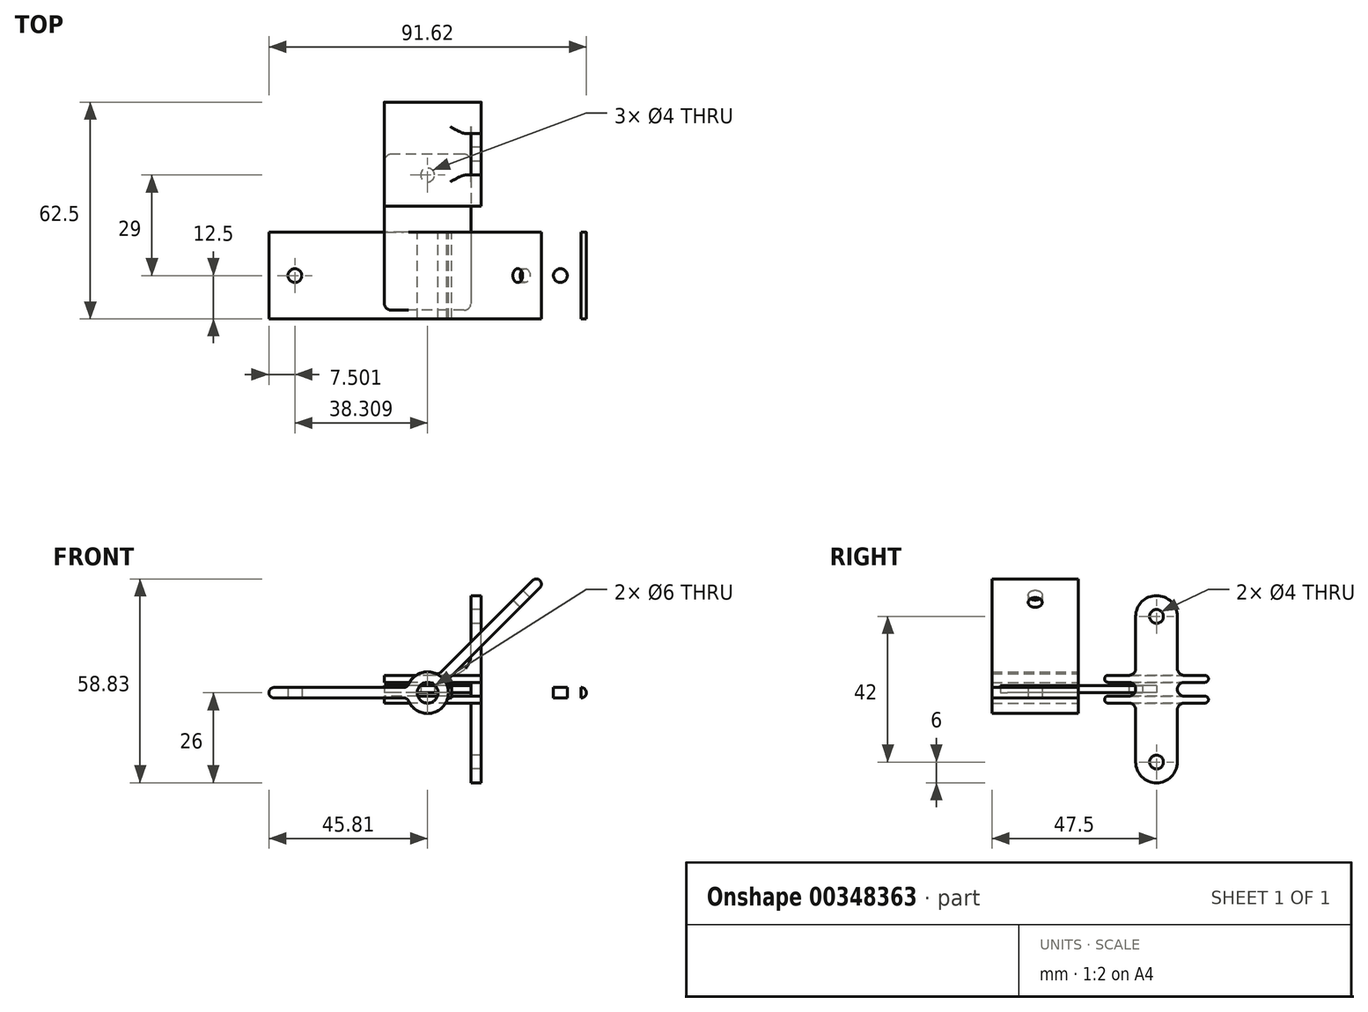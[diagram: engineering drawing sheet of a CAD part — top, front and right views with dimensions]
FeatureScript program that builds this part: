
annotation { "Feature Type Name" : "Feature", "Feature Type Description" : "" }
export const myFeature = defineFeature(function(context is Context, id is Id, definition is map)
    precondition{}
    {
        {
            var Q0;
            Q0=qCreatedBy(makeId("Front.planeOp"),FACE);
            var sketch = newSketch(context, id + "F0", { "sketchPlane" : qUnion([Q0])});
            skCircle(sketch, "E0", {"center": v(0, 0) * mm, "radius": 3 * mm});
            skCircle(sketch, "E1", {"center": v(0, 0) * mm, "radius": 6 * mm});
            skLineSegment(sketch, "E2", {"start": v(-5.8, 1.5) * mm, "end": v(-45.8, 1.5) * mm});
            skLineSegment(sketch, "E3", {"start": v(-45.8, 1.5) * mm, "end": v(-45.8, -1.5) * mm});
            skLineSegment(sketch, "E4", {"start": v(-45.8, -1.5) * mm, "end": v(-5.8, -1.5) * mm});
            skLineSegment(sketch, "E5.MirrorCS", {"start": v(45.8, -1.5) * mm, "end": v(5.8, -1.5) * mm});
            skLineSegment(sketch, "E6.MirrorCS", {"start": v(45.8, 1.5) * mm, "end": v(45.8, -1.5) * mm});
            skLineSegment(sketch, "E7.MirrorCS", {"start": v(5.8, 1.5) * mm, "end": v(45.8, 1.5) * mm});
            skSolve(sketch);
        }
        {
            var Q0;
            {var subQ0=sQuery(id+"F0.wireOp",EDGE,"E2");Q0=makeQuery(id+"F0.imprint","IMPRINT",FACE,{"disambiguationData":[TD([[makeQuery(id+"F0.imprint","IMPRINT",EDGE,{"derivedFrom":subQ0}),1.0]])]});}
            var Q1;
            Q1=makeQuery(id+"F0.imprint","IMPRINT",FACE,{"disambiguationData":[TD([[makeQuery(id+"F0.imprint","IMPRINT",EDGE,{"derivedFrom":sQuery(id+"F0.wireOp",EDGE,"E0")}),-1.0]])]});
            var Q2;
            {var subQ0=sQuery(id+"F0.wireOp",EDGE,"E5.MirrorCS");Q2=makeQuery(id+"F0.imprint","IMPRINT",FACE,{"disambiguationData":[TD([[makeQuery(id+"F0.imprint","IMPRINT",EDGE,{"derivedFrom":subQ0}),-1.0]])]});}
            extrude(context, id + "F1", {"entities" : qUnion([Q0, Q1, Q2]), "depth" : 25 * mm});
        }
        {
            var Q0;
            Q0=makeQuery(id+"F1.opExtrude","SWEPT_EDGE",EDGE,{"disambiguationData":[OSD([sQuery(id+"F0.wireOp",EDGE,"E2"),sQuery(id+"F0.wireOp",EDGE,"E3")])]});
            var Q1;
            Q1=makeQuery(id+"F1.opExtrude","SWEPT_EDGE",EDGE,{"disambiguationData":[OSD([sQuery(id+"F0.wireOp",EDGE,"E3"),sQuery(id+"F0.wireOp",EDGE,"E4")])]});
            var Q2;
            Q2=makeQuery(id+"F1.opExtrude","SWEPT_EDGE",EDGE,{"disambiguationData":[OSD([sQuery(id+"F0.wireOp",EDGE,"E6.MirrorCS"),sQuery(id+"F0.wireOp",EDGE,"E7.MirrorCS")])]});
            var Q3;
            Q3=makeQuery(id+"F1.opExtrude","SWEPT_EDGE",EDGE,{"disambiguationData":[OSD([sQuery(id+"F0.wireOp",EDGE,"E5.MirrorCS"),sQuery(id+"F0.wireOp",EDGE,"E6.MirrorCS")])]});
            var Q4;
            Q4=makeQuery(id+"F1.opExtrude","SWEPT_EDGE",EDGE,{"disambiguationData":[OSD([sQuery(id+"F0.wireOp",EDGE,"E1"),sQuery(id+"F0.wireOp",EDGE,"E2")])]});
            var Q5;
            Q5=makeQuery(id+"F1.opExtrude","SWEPT_EDGE",EDGE,{"disambiguationData":[OSD([sQuery(id+"F0.wireOp",EDGE,"E1"),sQuery(id+"F0.wireOp",EDGE,"E7.MirrorCS")])]});
            var Q6;
            Q6=makeQuery(id+"F1.opExtrude","SWEPT_EDGE",EDGE,{"disambiguationData":[OSD([sQuery(id+"F0.wireOp",EDGE,"E1"),sQuery(id+"F0.wireOp",EDGE,"E4")])]});
            var Q7;
            Q7=makeQuery(id+"F1.opExtrude","SWEPT_EDGE",EDGE,{"disambiguationData":[OSD([sQuery(id+"F0.wireOp",EDGE,"E1"),sQuery(id+"F0.wireOp",EDGE,"E5.MirrorCS")])]});
            fillet(context, id + "F2", {"entities" : qUnion([Q0, Q1, Q2, Q3, Q4, Q5, Q6, Q7]), "radius" : 1.5 * mm, "tangentPropagation" : true, "allowEdgeOverflow" : false});
        }
        {
            var Q0;
            Q0=qCreatedBy(makeId("Front.planeOp"),FACE);
            var sketch = newSketch(context, id + "F3", { "sketchPlane" : qUnion([Q0])});
            skCircle(sketch, "E8", {"center": v(0, 0) * mm, "radius": 3 * mm});
            skCircle(sketch, "E9", {"center": v(0, 0) * mm, "radius": 6 * mm});
            skLineSegment(sketch, "E10", {"start": v(-5.8, 1.5) * mm, "end": v(-45.8, 1.5) * mm});
            skLineSegment(sketch, "E11", {"start": v(-45.8, 1.5) * mm, "end": v(-45.8, -1.5) * mm});
            skLineSegment(sketch, "E12", {"start": v(-45.8, -1.5) * mm, "end": v(-5.8, -1.5) * mm});
            skLineSegment(sketch, "E13", {"start": v(0, 0) * mm, "end": v(32.4, 32.4) * mm, "construction": true});
            skLineSegment(sketch, "E14", {"start": v(3.05, 5.17) * mm, "end": v(31.33, 33.45) * mm});
            skLineSegment(sketch, "E15", {"start": v(31.33, 33.45) * mm, "end": v(33.45, 31.33) * mm});
            skLineSegment(sketch, "E16", {"start": v(33.45, 31.33) * mm, "end": v(5.17, 3.05) * mm});
            skSolve(sketch);
        }
        {
            var Q0;
            {var subQ0=sQuery(id+"F3.wireOp",EDGE,"E10");Q0=makeQuery(id+"F3.imprint","IMPRINT",FACE,{"disambiguationData":[TD([[makeQuery(id+"F3.imprint","IMPRINT",EDGE,{"derivedFrom":subQ0}),1.0]])]});}
            var Q1;
            Q1=makeQuery(id+"F3.imprint","IMPRINT",FACE,{"disambiguationData":[TD([[makeQuery(id+"F3.imprint","IMPRINT",EDGE,{"derivedFrom":sQuery(id+"F3.wireOp",EDGE,"E8")}),-1.0]])]});
            var Q2;
            {var subQ0=sQuery(id+"F3.wireOp",EDGE,"E14");Q2=makeQuery(id+"F3.imprint","IMPRINT",FACE,{"disambiguationData":[TD([[makeQuery(id+"F3.imprint","IMPRINT",EDGE,{"derivedFrom":subQ0}),-1.0]])]});}
            extrude(context, id + "F4", {"entities" : qUnion([Q0, Q1, Q2]), "depth" : 25 * mm});
        }
        {
            var Q0;
            Q0=makeQuery(id+"F4.opExtrude","SWEPT_EDGE",EDGE,{"disambiguationData":[OSD([sQuery(id+"F3.wireOp",EDGE,"E10"),sQuery(id+"F3.wireOp",EDGE,"E11")])]});
            var Q1;
            Q1=makeQuery(id+"F4.opExtrude","SWEPT_EDGE",EDGE,{"disambiguationData":[OSD([sQuery(id+"F3.wireOp",EDGE,"E9"),sQuery(id+"F3.wireOp",EDGE,"E10")])]});
            var Q2;
            Q2=makeQuery(id+"F4.opExtrude","SWEPT_EDGE",EDGE,{"disambiguationData":[OSD([sQuery(id+"F3.wireOp",EDGE,"E9"),sQuery(id+"F3.wireOp",EDGE,"E14")])]});
            var Q3;
            Q3=makeQuery(id+"F4.opExtrude","SWEPT_EDGE",EDGE,{"disambiguationData":[OSD([sQuery(id+"F3.wireOp",EDGE,"E14"),sQuery(id+"F3.wireOp",EDGE,"E15")])]});
            var Q4;
            Q4=makeQuery(id+"F4.opExtrude","SWEPT_EDGE",EDGE,{"disambiguationData":[OSD([sQuery(id+"F3.wireOp",EDGE,"E15"),sQuery(id+"F3.wireOp",EDGE,"E16")])]});
            var Q5;
            Q5=makeQuery(id+"F4.opExtrude","SWEPT_EDGE",EDGE,{"disambiguationData":[OSD([sQuery(id+"F3.wireOp",EDGE,"E11"),sQuery(id+"F3.wireOp",EDGE,"E12")])]});
            var Q6;
            Q6=makeQuery(id+"F4.opExtrude","SWEPT_EDGE",EDGE,{"disambiguationData":[OSD([sQuery(id+"F3.wireOp",EDGE,"E9"),sQuery(id+"F3.wireOp",EDGE,"E12")])]});
            var Q7;
            Q7=makeQuery(id+"F4.opExtrude","SWEPT_EDGE",EDGE,{"disambiguationData":[OSD([sQuery(id+"F3.wireOp",EDGE,"E9"),sQuery(id+"F3.wireOp",EDGE,"E16")])]});
            fillet(context, id + "F5", {"entities" : qUnion([Q0, Q1, Q2, Q3, Q4, Q5, Q6, Q7]), "radius" : 1.5 * mm, "tangentPropagation" : true, "allowEdgeOverflow" : false});
        }
        {
            var Q0;
            Q0=makeQuery(id+"F4.opExtrude","SWEPT_FACE",FACE,{"disambiguationData":[OSD([sQuery(id+"F3.wireOp",EDGE,"E12")])]});
            var sketch = newSketch(context, id + "F6", { "sketchPlane" : qUnion([Q0])});
            skLineSegment(sketch, "E17.0", {"start": v(-44.3, 25) * mm, "end": v(-44.3, 0) * mm});
            skCircle(sketch, "E18", {"center": v(-38.3, 12.5) * mm, "radius": 2 * mm});
            skPoint(sketch, "E18.centerSnap0", {"position": v(-44.3, 12.5) * mm});
            skSolve(sketch);
        }
        {
            var Q0;
            Q0=makeQuery(id+"F4.opExtrude","SWEPT_FACE",FACE,{"disambiguationData":[OSD([sQuery(id+"F3.wireOp",EDGE,"E16")])]});
            var sketch = newSketch(context, id + "F7", { "sketchPlane" : qUnion([Q0])});
            skLineSegment(sketch, "E19.0", {"start": v(0, 44.3) * mm, "end": v(-25, 44.3) * mm});
            skCircle(sketch, "E20", {"center": v(-12.5, 38.3) * mm, "radius": 2 * mm});
            skPoint(sketch, "E20.centerSnap0", {"position": v(-12.5, 44.3) * mm});
            skSolve(sketch);
        }
        {
            var Q0;
            Q0=makeQuery(id+"F7.imprint","IMPRINT",FACE,{"disambiguationData":[TD([[makeQuery(id+"F7.imprint","IMPRINT",EDGE,{"derivedFrom":sQuery(id+"F7.wireOp",EDGE,"E20")}),1.0]])]});
            extrude(context, id + "F8", {"entities" : qUnion([Q0]), "operationType" : NewBodyOperationType.REMOVE, "endBound" : BoundingType.UP_TO_NEXT, "oppositeDirection" : true, "depth" : 25 * mm});
        }
        {
            var Q0;
            Q0=makeQuery(id+"F1.opExtrude","SWEPT_FACE",FACE,{"disambiguationData":[OSD([sQuery(id+"F0.wireOp",EDGE,"E5.MirrorCS")])]});
            var sketch = newSketch(context, id + "F9", { "sketchPlane" : qUnion([Q0])});
            skCircle(sketch, "E21.0", {"center": v(-38.3, 12.5) * mm, "radius": 2 * mm});
            skCircle(sketch, "E22.MirrorC", {"center": v(38.3, 12.5) * mm, "radius": 2 * mm});
            skSolve(sketch);
        }
        {
            var Q0;
            Q0=makeQuery(id+"F6.imprint","IMPRINT",FACE,{"disambiguationData":[TD([[makeQuery(id+"F6.imprint","IMPRINT",EDGE,{"derivedFrom":sQuery(id+"F6.wireOp",EDGE,"E18")}),1.0]])]});
            var Q1;
            Q1=makeQuery(id+"F9.imprint","IMPRINT",FACE,{"disambiguationData":[TD([[makeQuery(id+"F9.imprint","IMPRINT",EDGE,{"derivedFrom":sQuery(id+"F9.wireOp",EDGE,"E22.MirrorC")}),-1.0]])]});
            extrude(context, id + "F10", {"entities" : qUnion([Q0, Q1]), "operationType" : NewBodyOperationType.REMOVE, "endBound" : BoundingType.UP_TO_NEXT, "oppositeDirection" : true, "depth" : 25 * mm});
        }
        {
            var Q0;
            Q0=qCreatedBy(makeId("Top.planeOp"),FACE);
            var sketch = newSketch(context, id + "F11", { "sketchPlane" : qUnion([Q0])});
            skLineSegment(sketch, "E23.bottom", {"start": v(12.5, 22.5) * mm, "end": v(-12.5, 22.5) * mm});
            skLineSegment(sketch, "E23.top", {"start": v(12.5, -22.5) * mm, "end": v(-12.5, -22.5) * mm});
            skLineSegment(sketch, "E23.left", {"start": v(12.5, 22.5) * mm, "end": v(12.5, -22.5) * mm});
            skLineSegment(sketch, "E23.right", {"start": v(-12.5, 22.5) * mm, "end": v(-12.5, -22.5) * mm});
            skPoint(sketch, "E23.middle", {"position": v(0, 0) * mm});
            skCircle(sketch, "E24", {"center": v(0, 16.5) * mm, "radius": 2 * mm});
            skSolve(sketch);
        }
        {
            var Q0;
            Q0=makeQuery(id+"F11.imprint","IMPRINT",FACE,{"disambiguationData":[TD([[makeQuery(id+"F11.imprint","IMPRINT",EDGE,{"derivedFrom":sQuery(id+"F11.wireOp",EDGE,"E23.bottom")}),1.0]])]});
            extrude(context, id + "F12", {"entities" : qUnion([Q0]), "depth" : 2 * mm});
        }
        {
            var Q0;
            Q0=makeQuery(id+"F12.opExtrude","SWEPT_FACE",FACE,{"disambiguationData":[OSD([sQuery(id+"F11.wireOp",EDGE,"E23.left")])]});
            var sketch = newSketch(context, id + "F13", { "sketchPlane" : qUnion([Q0])});
            skLineSegment(sketch, "E25.0", {"start": v(22.5, 0) * mm, "end": v(-22.5, 0) * mm});
            skLineSegment(sketch, "E25.1", {"start": v(22.5, 2) * mm, "end": v(-22.5, 2) * mm});
            skLineSegment(sketch, "E26.bottom", {"start": v(7.5, 5) * mm, "end": v(37.5, 5) * mm});
            skLineSegment(sketch, "E26.top", {"start": v(7.5, -3) * mm, "end": v(37.5, -3) * mm});
            skLineSegment(sketch, "E26.left", {"start": v(7.5, 5) * mm, "end": v(7.5, -3) * mm});
            skLineSegment(sketch, "E26.right", {"start": v(37.5, 5) * mm, "end": v(37.5, -3) * mm});
            skPoint(sketch, "E26.middle", {"position": v(22.5, 1) * mm});
            skLineSegment(sketch, "E27", {"start": v(7.5, 3) * mm, "end": v(37.5, 3) * mm});
            skLineSegment(sketch, "E28", {"start": v(7.5, -1) * mm, "end": v(37.5, -1) * mm});
            skLineSegment(sketch, "E29", {"start": v(7.5, 1) * mm, "end": v(37.5, 1) * mm, "construction": true});
            skLineSegment(sketch, "E30.bottom", {"start": v(16.5, -26) * mm, "end": v(28.5, -26) * mm});
            skLineSegment(sketch, "E30.top", {"start": v(16.5, 28) * mm, "end": v(28.5, 28) * mm});
            skLineSegment(sketch, "E30.left", {"start": v(16.5, -26) * mm, "end": v(16.5, 28) * mm});
            skLineSegment(sketch, "E30.right", {"start": v(28.5, -26) * mm, "end": v(28.5, 28) * mm});
            skCircle(sketch, "E31", {"center": v(22.5, 22) * mm, "radius": 2 * mm});
            skCircle(sketch, "E32.MirrorC", {"center": v(22.5, -20) * mm, "radius": 2 * mm});
            skSolve(sketch);
        }
        {
            var Q0;
            {var subQ1=sQuery(id+"F13.wireOp",EDGE,"E30.top");Q0=makeQuery(id+"F13.imprint","IMPRINT",FACE,{"disambiguationData":[TD([[makeQuery(id+"F13.imprint","IMPRINT",EDGE,{"derivedFrom":subQ1}),-1.0]])]});}
            var Q1;
            {var subQ1=sQuery(id+"F13.wireOp",EDGE,"E30.bottom");Q1=makeQuery(id+"F13.imprint","IMPRINT",FACE,{"disambiguationData":[TD([[makeQuery(id+"F13.imprint","IMPRINT",EDGE,{"derivedFrom":subQ1}),1.0]])]});}
            var Q2;
            {var subQ0=sQuery(id+"F13.wireOp",EDGE,"E26.right");var subQ1=sQuery(id+"F13.wireOp",EDGE,"E26.bottom");var subQ2=makeQuery(id+"F13.imprint","INTERSECT",VERTEX,{"derivedFrom":[subQ1,subQ0]});Q2=makeQuery(id+"F13.imprint","IMPRINT",FACE,{"disambiguationData":[TD([[makeQuery(id+"F13.imprint","IMPRINT",EDGE,{"disambiguationData":[TD([[subQ2,1.0]])],"derivedFrom":subQ1}),-1.0]])]});}
            var Q3;
            {var subQ0=sQuery(id+"F13.wireOp",EDGE,"E30.left");var subQ1=sQuery(id+"F13.wireOp",EDGE,"E26.bottom");var subQ2=makeQuery(id+"F13.imprint","INTERSECT",VERTEX,{"derivedFrom":[subQ1,subQ0]});Q3=makeQuery(id+"F13.imprint","IMPRINT",FACE,{"disambiguationData":[TD([[makeQuery(id+"F13.imprint","IMPRINT",EDGE,{"disambiguationData":[TD([[subQ2,-1.0]])],"derivedFrom":subQ1}),-1.0]])]});}
            var Q4;
            {var subQ0=sQuery(id+"F13.wireOp",EDGE,"E26.left");var subQ1=sQuery(id+"F13.wireOp",EDGE,"E26.bottom");var subQ2=makeQuery(id+"F13.imprint","INTERSECT",VERTEX,{"derivedFrom":[subQ1,subQ0]});Q4=makeQuery(id+"F13.imprint","IMPRINT",FACE,{"disambiguationData":[TD([[makeQuery(id+"F13.imprint","IMPRINT",EDGE,{"disambiguationData":[TD([[subQ2,-1.0]])],"derivedFrom":subQ1}),-1.0]])]});}
            var Q5;
            {var subQ0=sQuery(id+"F13.wireOp",EDGE,"E26.left");var subQ1=sQuery(id+"F13.wireOp",EDGE,"E26.top");var subQ2=makeQuery(id+"F13.imprint","INTERSECT",VERTEX,{"derivedFrom":[subQ1,subQ0]});Q5=makeQuery(id+"F13.imprint","IMPRINT",FACE,{"disambiguationData":[TD([[makeQuery(id+"F13.imprint","IMPRINT",EDGE,{"disambiguationData":[TD([[subQ2,-1.0]])],"derivedFrom":subQ1}),1.0]])]});}
            var Q6;
            {var subQ0=sQuery(id+"F13.wireOp",EDGE,"E30.left");var subQ1=sQuery(id+"F13.wireOp",EDGE,"E26.top");var subQ2=makeQuery(id+"F13.imprint","INTERSECT",VERTEX,{"derivedFrom":[subQ1,subQ0]});Q6=makeQuery(id+"F13.imprint","IMPRINT",FACE,{"disambiguationData":[TD([[makeQuery(id+"F13.imprint","IMPRINT",EDGE,{"disambiguationData":[TD([[subQ2,-1.0]])],"derivedFrom":subQ1}),1.0]])]});}
            var Q7;
            {var subQ0=sQuery(id+"F13.wireOp",EDGE,"E26.right");var subQ1=sQuery(id+"F13.wireOp",EDGE,"E26.top");var subQ2=makeQuery(id+"F13.imprint","INTERSECT",VERTEX,{"derivedFrom":[subQ1,subQ0]});Q7=makeQuery(id+"F13.imprint","IMPRINT",FACE,{"disambiguationData":[TD([[makeQuery(id+"F13.imprint","IMPRINT",EDGE,{"disambiguationData":[TD([[subQ2,1.0]])],"derivedFrom":subQ1}),1.0]])]});}
            var Q8;
            {var subQ10=makeQuery(id+"F12.opExtrude","SWEPT_EDGE",EDGE,{"disambiguationData":[OSD([sQuery(id+"F11.wireOp",EDGE,"E23.bottom"),sQuery(id+"F11.wireOp",EDGE,"E23.left")])]});Q8=makeQuery(id+"F13.imprint","IMPRINT",FACE,{"disambiguationData":[TD([[makeQuery(id+"F13.imprint","IMPRINT",EDGE,{"derivedFrom":subQ10}),1.0]])]});}
            var Q9;
            {var subQ1=makeQuery(id+"F12.opExtrude","SWEPT_EDGE",EDGE,{"disambiguationData":[OSD([sQuery(id+"F11.wireOp",EDGE,"E23.bottom"),sQuery(id+"F11.wireOp",EDGE,"E23.left")])]});Q9=makeQuery(id+"F13.imprint","IMPRINT",FACE,{"disambiguationData":[TD([[makeQuery(id+"F13.imprint","IMPRINT",EDGE,{"derivedFrom":subQ1}),-1.0]])]});}
            extrude(context, id + "F14", {"entities" : qUnion([Q0, Q1, Q2, Q3, Q4, Q5, Q6, Q7, Q8, Q9]), "depth" : 3 * mm});
        }
        {
            var Q0;
            {var subQ0=sQuery(id+"F13.wireOp",EDGE,"E30.left");var subQ1=sQuery(id+"F13.wireOp",EDGE,"E26.bottom");var subQ2=makeQuery(id+"F13.imprint","INTERSECT",VERTEX,{"derivedFrom":[subQ1,subQ0]});Q0=makeQuery(id+"F13.imprint","IMPRINT",FACE,{"disambiguationData":[TD([[makeQuery(id+"F13.imprint","IMPRINT",EDGE,{"disambiguationData":[TD([[subQ2,-1.0]])],"derivedFrom":subQ1}),-1.0]])]});}
            var Q1;
            {var subQ0=sQuery(id+"F13.wireOp",EDGE,"E26.left");var subQ1=sQuery(id+"F13.wireOp",EDGE,"E26.bottom");var subQ2=makeQuery(id+"F13.imprint","INTERSECT",VERTEX,{"derivedFrom":[subQ1,subQ0]});Q1=makeQuery(id+"F13.imprint","IMPRINT",FACE,{"disambiguationData":[TD([[makeQuery(id+"F13.imprint","IMPRINT",EDGE,{"disambiguationData":[TD([[subQ2,-1.0]])],"derivedFrom":subQ1}),-1.0]])]});}
            var Q2;
            {var subQ0=sQuery(id+"F13.wireOp",EDGE,"E26.right");var subQ1=sQuery(id+"F13.wireOp",EDGE,"E26.bottom");var subQ2=makeQuery(id+"F13.imprint","INTERSECT",VERTEX,{"derivedFrom":[subQ1,subQ0]});Q2=makeQuery(id+"F13.imprint","IMPRINT",FACE,{"disambiguationData":[TD([[makeQuery(id+"F13.imprint","IMPRINT",EDGE,{"disambiguationData":[TD([[subQ2,1.0]])],"derivedFrom":subQ1}),-1.0]])]});}
            var Q3;
            {var subQ0=sQuery(id+"F13.wireOp",EDGE,"E26.right");var subQ1=sQuery(id+"F13.wireOp",EDGE,"E26.top");var subQ2=makeQuery(id+"F13.imprint","INTERSECT",VERTEX,{"derivedFrom":[subQ1,subQ0]});Q3=makeQuery(id+"F13.imprint","IMPRINT",FACE,{"disambiguationData":[TD([[makeQuery(id+"F13.imprint","IMPRINT",EDGE,{"disambiguationData":[TD([[subQ2,1.0]])],"derivedFrom":subQ1}),1.0]])]});}
            var Q4;
            {var subQ0=sQuery(id+"F13.wireOp",EDGE,"E30.left");var subQ1=sQuery(id+"F13.wireOp",EDGE,"E26.top");var subQ2=makeQuery(id+"F13.imprint","INTERSECT",VERTEX,{"derivedFrom":[subQ1,subQ0]});Q4=makeQuery(id+"F13.imprint","IMPRINT",FACE,{"disambiguationData":[TD([[makeQuery(id+"F13.imprint","IMPRINT",EDGE,{"disambiguationData":[TD([[subQ2,-1.0]])],"derivedFrom":subQ1}),1.0]])]});}
            var Q5;
            {var subQ0=sQuery(id+"F13.wireOp",EDGE,"E26.left");var subQ1=sQuery(id+"F13.wireOp",EDGE,"E26.top");var subQ2=makeQuery(id+"F13.imprint","INTERSECT",VERTEX,{"derivedFrom":[subQ1,subQ0]});Q5=makeQuery(id+"F13.imprint","IMPRINT",FACE,{"disambiguationData":[TD([[makeQuery(id+"F13.imprint","IMPRINT",EDGE,{"disambiguationData":[TD([[subQ2,-1.0]])],"derivedFrom":subQ1}),1.0]])]});}
            var Q6;
            Q6=makeQuery(id+"F12.opExtrude","SWEPT_FACE",FACE,{"disambiguationData":[OSD([sQuery(id+"F11.wireOp",EDGE,"E23.right")])]});
            extrude(context, id + "F15", {"entities" : qUnion([Q0, Q1, Q2, Q3, Q4, Q5]), "operationType" : NewBodyOperationType.ADD, "endBound" : BoundingType.UP_TO_SURFACE, "oppositeDirection" : true, "endBoundEntityFace" : qUnion([Q6]), "depth" : 25 * mm});
        }
        {
            var Q0;
            {var subQ0=sQuery(id+"F13.wireOp",EDGE,"E26.left");var subQ1=sQuery(id+"F13.wireOp",EDGE,"E26.bottom");Q0=makeQuery(id+"F15.boolean.opBoolean","MERGE",EDGE,{"derivedFrom":[makeQuery(id+"F14.opExtrude","SWEPT_EDGE",EDGE,{"disambiguationData":[OSD([subQ1,subQ0])]}),makeQuery(id+"F15.opExtrude","SWEPT_EDGE",EDGE,{"disambiguationData":[OSD([subQ1,subQ0])]})]});}
            var Q1;
            {var subQ0=sQuery(id+"F13.wireOp",EDGE,"E27");var subQ1=sQuery(id+"F13.wireOp",EDGE,"E26.left");Q1=makeQuery(id+"F15.boolean.opBoolean","MERGE",EDGE,{"derivedFrom":[makeQuery(id+"F14.opExtrude","SWEPT_EDGE",EDGE,{"disambiguationData":[OSD([subQ1,subQ0])]}),makeQuery(id+"F15.opExtrude","SWEPT_EDGE",EDGE,{"disambiguationData":[OSD([subQ1,subQ0])]})]});}
            var Q2;
            {var subQ0=sQuery(id+"F13.wireOp",EDGE,"E26.right");var subQ1=sQuery(id+"F13.wireOp",EDGE,"E26.bottom");Q2=makeQuery(id+"F15.boolean.opBoolean","MERGE",EDGE,{"derivedFrom":[makeQuery(id+"F14.opExtrude","SWEPT_EDGE",EDGE,{"disambiguationData":[OSD([subQ1,subQ0])]}),makeQuery(id+"F15.opExtrude","SWEPT_EDGE",EDGE,{"disambiguationData":[OSD([subQ1,subQ0])]})]});}
            var Q3;
            {var subQ0=sQuery(id+"F13.wireOp",EDGE,"E27");var subQ1=sQuery(id+"F13.wireOp",EDGE,"E26.right");Q3=makeQuery(id+"F15.boolean.opBoolean","MERGE",EDGE,{"derivedFrom":[makeQuery(id+"F14.opExtrude","SWEPT_EDGE",EDGE,{"disambiguationData":[OSD([subQ1,subQ0])]}),makeQuery(id+"F15.opExtrude","SWEPT_EDGE",EDGE,{"disambiguationData":[OSD([subQ1,subQ0])]})]});}
            var Q4;
            {var subQ0=sQuery(id+"F13.wireOp",EDGE,"E28");var subQ1=sQuery(id+"F13.wireOp",EDGE,"E26.right");Q4=makeQuery(id+"F15.boolean.opBoolean","MERGE",EDGE,{"derivedFrom":[makeQuery(id+"F14.opExtrude","SWEPT_EDGE",EDGE,{"disambiguationData":[OSD([subQ1,subQ0])]}),makeQuery(id+"F15.opExtrude","SWEPT_EDGE",EDGE,{"disambiguationData":[OSD([subQ1,subQ0])]})]});}
            var Q5;
            {var subQ0=sQuery(id+"F13.wireOp",EDGE,"E26.right");var subQ1=sQuery(id+"F13.wireOp",EDGE,"E26.top");Q5=makeQuery(id+"F15.boolean.opBoolean","MERGE",EDGE,{"derivedFrom":[makeQuery(id+"F14.opExtrude","SWEPT_EDGE",EDGE,{"disambiguationData":[OSD([subQ1,subQ0])]}),makeQuery(id+"F15.opExtrude","SWEPT_EDGE",EDGE,{"disambiguationData":[OSD([subQ1,subQ0])]})]});}
            var Q6;
            {var subQ0=sQuery(id+"F13.wireOp",EDGE,"E26.left");var subQ1=sQuery(id+"F13.wireOp",EDGE,"E26.top");Q6=makeQuery(id+"F15.boolean.opBoolean","MERGE",EDGE,{"derivedFrom":[makeQuery(id+"F14.opExtrude","SWEPT_EDGE",EDGE,{"disambiguationData":[OSD([subQ1,subQ0])]}),makeQuery(id+"F15.opExtrude","SWEPT_EDGE",EDGE,{"disambiguationData":[OSD([subQ1,subQ0])]})]});}
            var Q7;
            {var subQ0=sQuery(id+"F13.wireOp",EDGE,"E28");var subQ1=sQuery(id+"F13.wireOp",EDGE,"E26.left");Q7=makeQuery(id+"F15.boolean.opBoolean","MERGE",EDGE,{"derivedFrom":[makeQuery(id+"F14.opExtrude","SWEPT_EDGE",EDGE,{"disambiguationData":[OSD([subQ1,subQ0])]}),makeQuery(id+"F15.opExtrude","SWEPT_EDGE",EDGE,{"disambiguationData":[OSD([subQ1,subQ0])]})]});}
            fillet(context, id + "F16", {"entities" : qUnion([Q0, Q1, Q2, Q3, Q4, Q5, Q6, Q7]), "radius" : 1 * mm, "tangentPropagation" : true, "allowEdgeOverflow" : false});
        }
        {
            var Q0;
            Q0=makeQuery(id+"F14.opExtrude","SWEPT_EDGE",EDGE,{"disambiguationData":[OSD([sQuery(id+"F13.wireOp",EDGE,"E30.bottom"),sQuery(id+"F13.wireOp",EDGE,"E30.left")])]});
            var Q1;
            Q1=makeQuery(id+"F14.opExtrude","SWEPT_EDGE",EDGE,{"disambiguationData":[OSD([sQuery(id+"F13.wireOp",EDGE,"E30.bottom"),sQuery(id+"F13.wireOp",EDGE,"E30.right")])]});
            var Q2;
            Q2=makeQuery(id+"F15.opExtrude","CAP_EDGE",EDGE,{"disambiguationData":[OSD([sQuery(id+"F13.wireOp",EDGE,"E26.top")])],"isStart":true});
            var Q3;
            Q3=makeQuery(id+"F15.opExtrude","CAP_EDGE",EDGE,{"disambiguationData":[OSD([sQuery(id+"F13.wireOp",EDGE,"E26.bottom")])],"isStart":true});
            var Q4;
            Q4=makeQuery(id+"F14.opExtrude","SWEPT_EDGE",EDGE,{"disambiguationData":[OSD([sQuery(id+"F13.wireOp",EDGE,"E30.top"),sQuery(id+"F13.wireOp",EDGE,"E30.right")])]});
            var Q5;
            Q5=makeQuery(id+"F14.opExtrude","SWEPT_EDGE",EDGE,{"disambiguationData":[OSD([sQuery(id+"F13.wireOp",EDGE,"E30.top"),sQuery(id+"F13.wireOp",EDGE,"E30.left")])]});
            fillet(context, id + "F17", {"entities" : qUnion([Q0, Q1, Q2, Q3, Q4, Q5]), "radius" : 6 * mm, "tangentPropagation" : true, "allowEdgeOverflow" : false});
        }
        {
            var Q0;
            Q0=makeQuery(id+"F14.opExtrude","SWEPT_EDGE",EDGE,{"disambiguationData":[OSD([sQuery(id+"F13.wireOp",EDGE,"E26.top"),sQuery(id+"F13.wireOp",EDGE,"E30.right")])]});
            var Q1;
            Q1=makeQuery(id+"F14.opExtrude","SWEPT_EDGE",EDGE,{"disambiguationData":[OSD([sQuery(id+"F13.wireOp",EDGE,"E26.top"),sQuery(id+"F13.wireOp",EDGE,"E30.left")])]});
            var Q2;
            Q2=makeQuery(id+"F14.opExtrude","SWEPT_EDGE",EDGE,{"disambiguationData":[OSD([sQuery(id+"F13.wireOp",EDGE,"E26.bottom"),sQuery(id+"F13.wireOp",EDGE,"E30.right")])]});
            var Q3;
            Q3=makeQuery(id+"F14.opExtrude","SWEPT_EDGE",EDGE,{"disambiguationData":[OSD([sQuery(id+"F13.wireOp",EDGE,"E26.bottom"),sQuery(id+"F13.wireOp",EDGE,"E30.left")])]});
            var Q4;
            Q4=makeQuery(id+"F14.opExtrude","SWEPT_EDGE",EDGE,{"disambiguationData":[OSD([sQuery(id+"F13.wireOp",EDGE,"E27"),sQuery(id+"F13.wireOp",EDGE,"E30.right")])]});
            var Q5;
            Q5=makeQuery(id+"F14.opExtrude","SWEPT_EDGE",EDGE,{"disambiguationData":[OSD([sQuery(id+"F13.wireOp",EDGE,"E28"),sQuery(id+"F13.wireOp",EDGE,"E30.right")])]});
            var Q6;
            Q6=makeQuery(id+"F14.opExtrude","SWEPT_EDGE",EDGE,{"disambiguationData":[OSD([sQuery(id+"F13.wireOp",EDGE,"E27"),sQuery(id+"F13.wireOp",EDGE,"E30.left")])]});
            var Q7;
            Q7=makeQuery(id+"F14.opExtrude","SWEPT_EDGE",EDGE,{"disambiguationData":[OSD([sQuery(id+"F13.wireOp",EDGE,"E28"),sQuery(id+"F13.wireOp",EDGE,"E30.left")])]});
            fillet(context, id + "F18", {"entities" : qUnion([Q0, Q1, Q2, Q3, Q4, Q5, Q6, Q7]), "radius" : 2 * mm, "tangentPropagation" : true, "allowEdgeOverflow" : false});
        }
        {
            var Q0;
            Q0=makeQuery(id+"F12.opExtrude","SWEPT_EDGE",EDGE,{"disambiguationData":[OSD([sQuery(id+"F11.wireOp",EDGE,"E23.top"),sQuery(id+"F11.wireOp",EDGE,"E23.right")])]});
            var Q1;
            Q1=makeQuery(id+"F12.opExtrude","SWEPT_EDGE",EDGE,{"disambiguationData":[OSD([sQuery(id+"F11.wireOp",EDGE,"E23.top"),sQuery(id+"F11.wireOp",EDGE,"E23.left")])]});
            var Q2;
            Q2=makeQuery(id+"F12.opExtrude","SWEPT_EDGE",EDGE,{"disambiguationData":[OSD([sQuery(id+"F11.wireOp",EDGE,"E23.bottom"),sQuery(id+"F11.wireOp",EDGE,"E23.left")])]});
            var Q3;
            Q3=makeQuery(id+"F12.opExtrude","SWEPT_EDGE",EDGE,{"disambiguationData":[OSD([sQuery(id+"F11.wireOp",EDGE,"E23.bottom"),sQuery(id+"F11.wireOp",EDGE,"E23.right")])]});
            fillet(context, id + "F19", {"entities" : qUnion([Q0, Q1, Q2, Q3]), "radius" : 2 * mm, "tangentPropagation" : true, "allowEdgeOverflow" : false});
        }
    });
